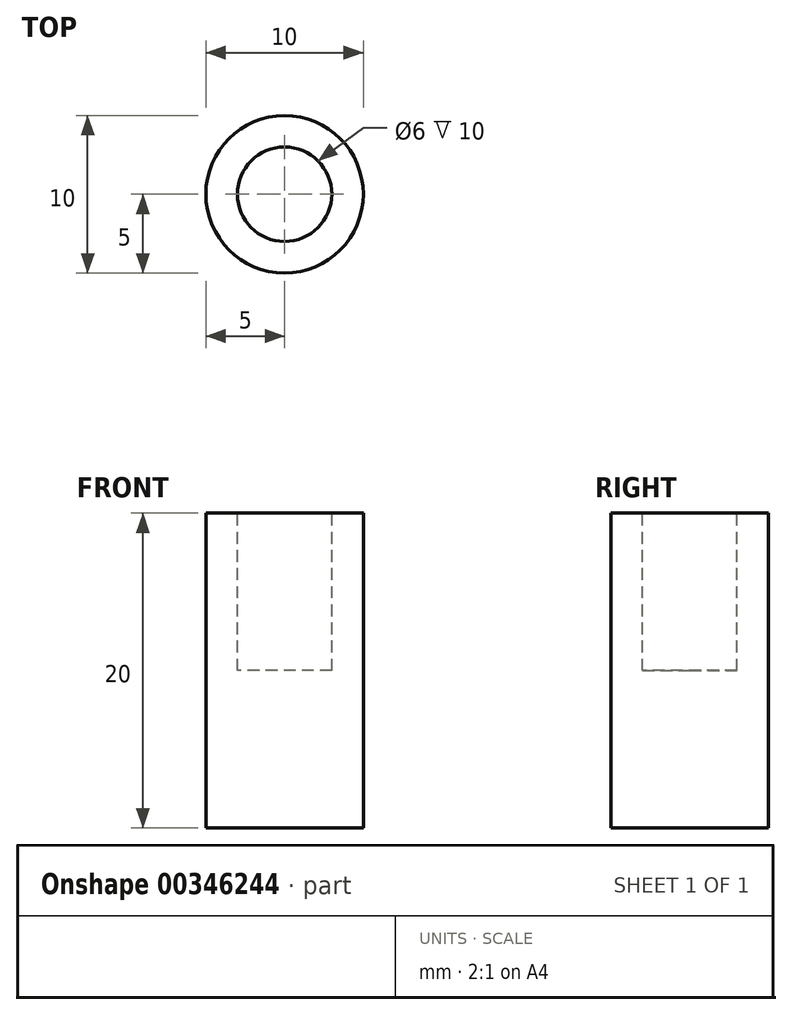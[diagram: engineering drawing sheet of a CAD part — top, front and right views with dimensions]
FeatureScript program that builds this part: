
annotation { "Feature Type Name" : "Feature", "Feature Type Description" : "" }
export const myFeature = defineFeature(function(context is Context, id is Id, definition is map)
    precondition{}
    {
        {
            var Q0;
            Q0=qCreatedBy(makeId("Top.planeOp"),FACE);
            var sketch = newSketch(context, id + "F0", { "sketchPlane" : qUnion([Q0])});
            skCircle(sketch, "E0", {"center": v(0, 0) * mm, "radius": 5 * mm});
            skCircle(sketch, "E1", {"center": v(0, 0) * mm, "radius": 2 * mm, "construction": true});
            skSolve(sketch);
        }
        {
            var Q0;
            Q0=makeQuery(id+"F0.imprint","IMPRINT",FACE,{"disambiguationData":[TD([[makeQuery(id+"F0.imprint","IMPRINT",EDGE,{"derivedFrom":sQuery(id+"F0.wireOp",EDGE,"E0")}),1.0]])]});
            extrude(context, id + "F1", {"entities" : qUnion([Q0]), "depth" : 20 * mm});
        }
        {
            var Q0;
            Q0=makeQuery(id+"F1.opExtrude","CAP_FACE",FACE,{"disambiguationData":[OSD([sQuery(id+"F0.wireOp",EDGE,"E0")])],"isStart":false});
            var sketch = newSketch(context, id + "F2", { "sketchPlane" : qUnion([Q0])});
            skCircle(sketch, "E2", {"center": v(0, 0) * mm, "radius": 3 * mm});
            skSolve(sketch);
        }
        {
            var Q0;
            Q0=makeQuery(id+"F2.imprint","IMPRINT",FACE,{"disambiguationData":[TD([[makeQuery(id+"F2.imprint","IMPRINT",EDGE,{"derivedFrom":sQuery(id+"F2.wireOp",EDGE,"E2")}),1.0]])]});
            extrude(context, id + "F3", {"entities" : qUnion([Q0]), "operationType" : NewBodyOperationType.REMOVE, "depth" : 10 * mm});
        }
        {
            var Q0;
            Q0 = qSketchRegion(id + "F2", true);
            extrude(context, id + "F4", {"entities" : qUnion([Q0]), "operationType" : NewBodyOperationType.REMOVE, "oppositeDirection" : true, "depth" : 10 * mm});
        }
    });
